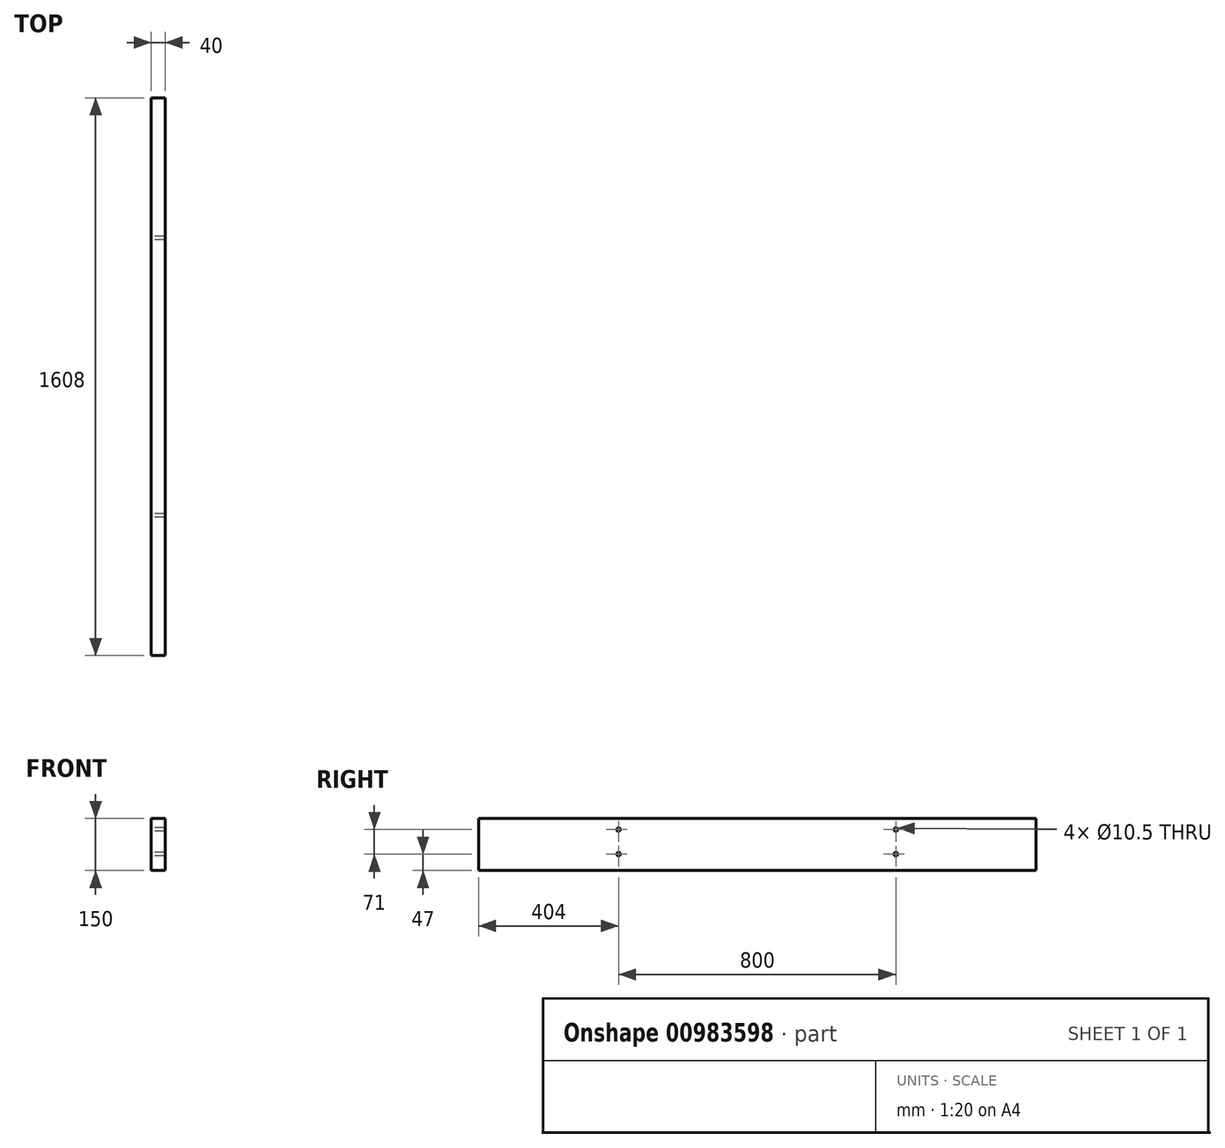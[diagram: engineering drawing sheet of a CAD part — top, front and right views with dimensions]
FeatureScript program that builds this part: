
annotation { "Feature Type Name" : "Feature", "Feature Type Description" : "" }
export const myFeature = defineFeature(function(context is Context, id is Id, definition is map)
    precondition{}
    {
        {
            var Q0;
            Q0=qCreatedBy(makeId("Front.planeOp"),FACE);
            var sketch = newSketch(context, id + "F0", { "sketchPlane" : qUnion([Q0])});
            skLineSegment(sketch, "E0.bottom", {"start": v(20, -75) * mm, "end": v(-20, -75) * mm});
            skLineSegment(sketch, "E0.top", {"start": v(20, 75) * mm, "end": v(-20, 75) * mm});
            skLineSegment(sketch, "E0.left", {"start": v(20, -75) * mm, "end": v(20, 75) * mm});
            skLineSegment(sketch, "E0.right", {"start": v(-20, -75) * mm, "end": v(-20, 75) * mm});
            skPoint(sketch, "E0.middle", {"position": v(0, 0) * mm});
            skSolve(sketch);
        }
        {
            var Q0;
            Q0=makeQuery(id+"F0.imprint","IMPRINT",FACE,{"disambiguationData":[TD([[makeQuery(id+"F0.imprint","IMPRINT",EDGE,{"derivedFrom":sQuery(id+"F0.wireOp",EDGE,"E0.bottom")}),-1.0]])]});
            extrude(context, id + "F1", {"entities" : qUnion([Q0]), "flatOperationType" : FlatOperationType.REMOVE, "depth" : 1608 * mm, "offsetDistance" : 25 * mm, "domain" : OperationDomain.MODEL, "symmetric" : true});
        }
        {
            var Q0;
            Q0=makeQuery(id+"F1.opExtrude","SWEPT_FACE",FACE,{"disambiguationData":[OSD([sQuery(id+"F0.wireOp",EDGE,"E0.left")])]});
            var sketch = newSketch(context, id + "F2", { "sketchPlane" : qUnion([Q0])});
            skLineSegment(sketch, "E1", {"start": v(0, 75) * mm, "end": v(0, -75) * mm, "construction": true});
            skLineSegment(sketch, "E2.bottom", {"start": v(400, -28) * mm, "end": v(-400, -28) * mm, "construction": true});
            skLineSegment(sketch, "E2.top", {"start": v(400, 43) * mm, "end": v(-400, 43) * mm, "construction": true});
            skLineSegment(sketch, "E2.left", {"start": v(400, -28) * mm, "end": v(400, 43) * mm, "construction": true});
            skLineSegment(sketch, "E2.right", {"start": v(-400, -28) * mm, "end": v(-400, 43) * mm, "construction": true});
            skPoint(sketch, "E2.middle", {"position": v(0, 7.5) * mm});
            skPoint(sketch, "E3", {"position": v(-400, 43) * mm});
            skPoint(sketch, "E4", {"position": v(-400, -28) * mm});
            skPoint(sketch, "E5", {"position": v(400, -28) * mm});
            skPoint(sketch, "E6", {"position": v(400, 43) * mm});
            skSolve(sketch);
        }
        {
            var Q0;
            Q0=sQuery(id+"F2.wireOp",VERTEX,"E3");
            var Q1;
            Q1=sQuery(id+"F2.wireOp",VERTEX,"E4");
            var Q2;
            Q2=sQuery(id+"F2.wireOp",VERTEX,"E5");
            var Q3;
            Q3=sQuery(id+"F2.wireOp",VERTEX,"E6");
            var Q4;
            Q4=makeQuery(id+"F1.opExtrude","SWEPT_BODY",BODY,{"disambiguationData":[OSD([sQuery(id+"F0.wireOp",EDGE,"E0.bottom"),sQuery(id+"F0.wireOp",EDGE,"E0.top"),sQuery(id+"F0.wireOp",EDGE,"E0.left"),sQuery(id+"F0.wireOp",EDGE,"E0.right")])]});
            hole(context, id + "F3", {"style" : HoleStyle.SIMPLE, "endStyle" : HoleEndStyle.THROUGH, "standardTappedOrClearance" : lookupTablePath({ "standard" : "ISO", "size" : "10.5", "type" : "Drilled" }), "standardBlindInLast" : lookupTablePath({ "standard" : "ISO", "size" : "10.5", "type" : "Drilled" }), "holeDiameter" : 10.5 * mm, "majorDiameter" : 5 * mm, "isTappedThrough" : true, "tappedDepth" : 19 * mm, "tapClearance" : 3, "startFromSketch" : true, "locations" : qUnion([Q0, Q1, Q2, Q3]), "scope" : qUnion([Q4])});
        }
    });
